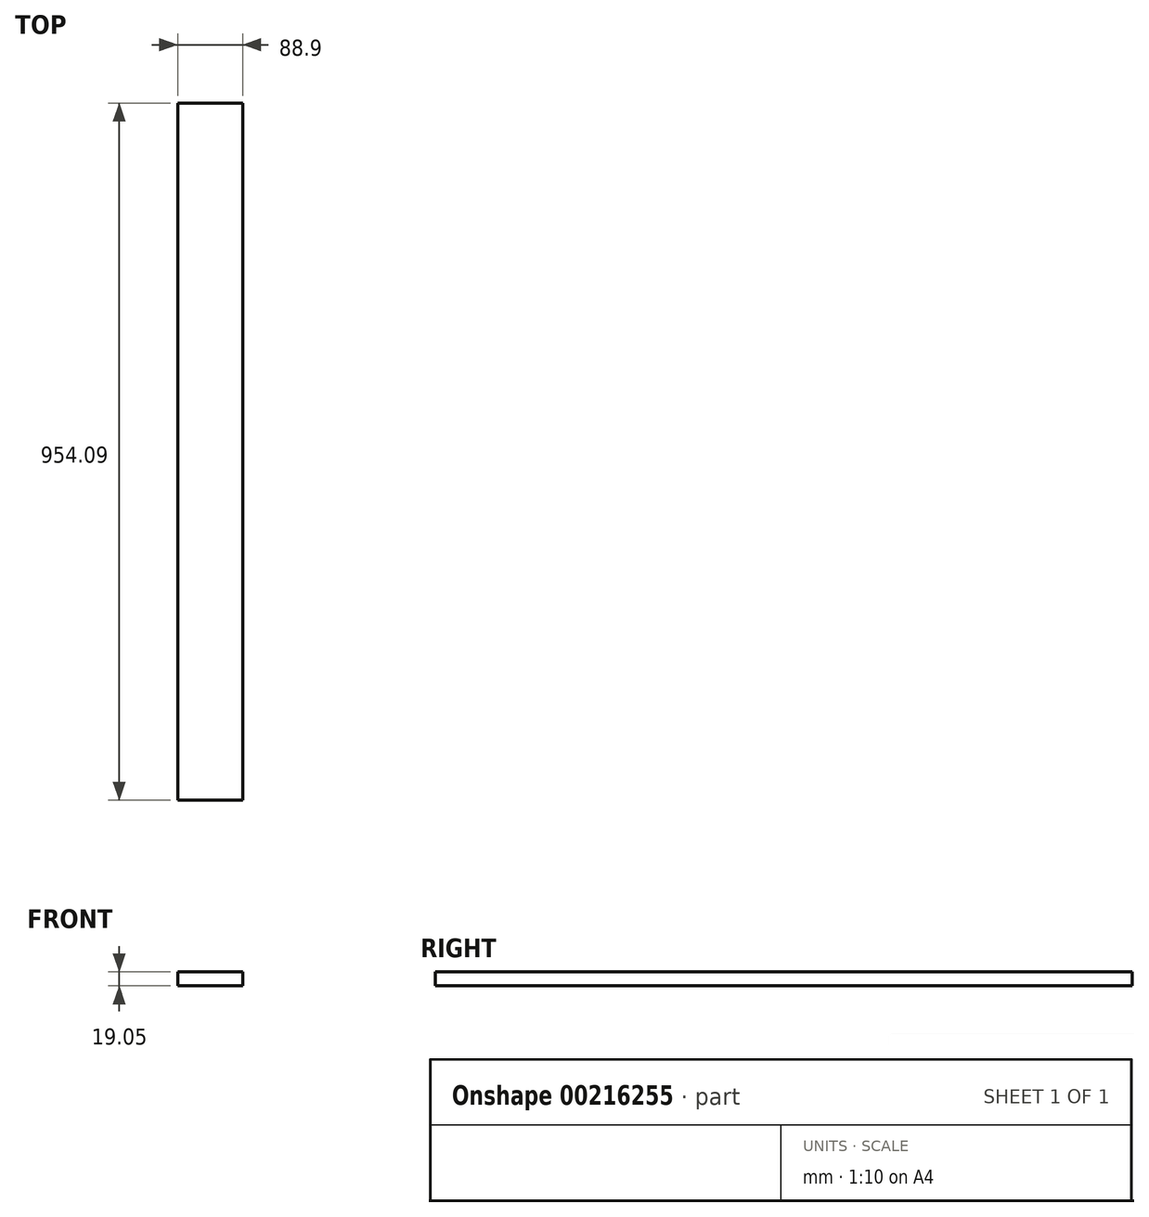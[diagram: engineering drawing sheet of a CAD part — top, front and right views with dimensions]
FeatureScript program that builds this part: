
annotation { "Feature Type Name" : "Feature", "Feature Type Description" : "" }
export const myFeature = defineFeature(function(context is Context, id is Id, definition is map)
    precondition{}
    {
        {
            var Q0;
            Q0=qCreatedBy(makeId("Top.planeOp"),FACE);
            var sketch = newSketch(context, id + "F0", { "sketchPlane" : qUnion([Q0])});
            skLineSegment(sketch, "E0", {"start": v(-1267.29, -1723.72) * mm, "end": v(-1178.39, -1723.72) * mm});
            skLineSegment(sketch, "E1", {"start": v(-1178.39, -1723.72) * mm, "end": v(-1178.39, -769.63) * mm});
            skLineSegment(sketch, "E2", {"start": v(-1178.39, -769.63) * mm, "end": v(-1267.29, -769.63) * mm});
            skLineSegment(sketch, "E3", {"start": v(-1267.29, -769.63) * mm, "end": v(-1267.29, -1723.72) * mm});
            skSolve(sketch);
        }
        {
            var Q0;
            Q0=makeQuery(id+"F0.imprint","IMPRINT",FACE,{"disambiguationData":[TD([[makeQuery(id+"F0.imprint","IMPRINT",EDGE,{"derivedFrom":sQuery(id+"F0.wireOp",EDGE,"E0")}),1.0]])]});
            extrude(context, id + "F1", {"entities" : qUnion([Q0]), "depth" : 19.05 * mm});
        }
    });
